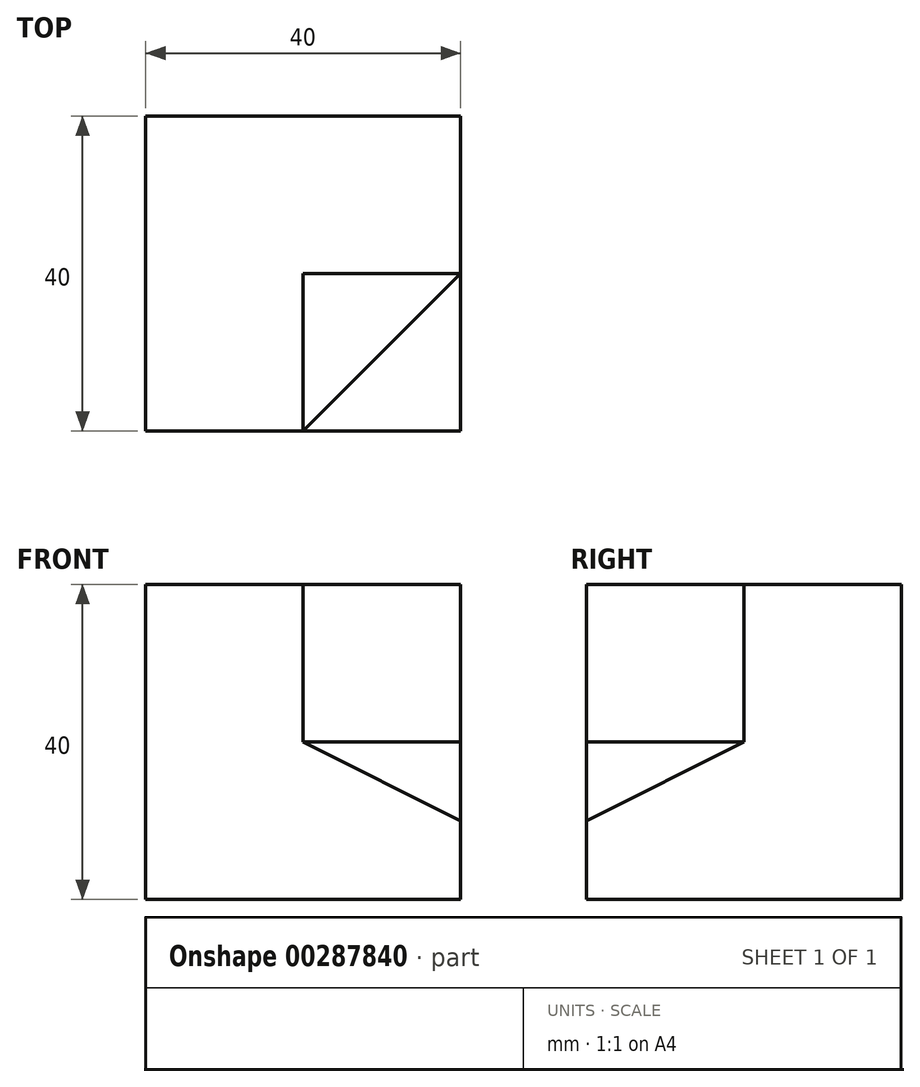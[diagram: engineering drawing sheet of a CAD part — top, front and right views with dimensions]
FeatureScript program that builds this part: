
annotation { "Feature Type Name" : "Feature", "Feature Type Description" : "" }
export const myFeature = defineFeature(function(context is Context, id is Id, definition is map)
    precondition{}
    {
        {
            var Q0;
            Q0=qCreatedBy(makeId("Front.planeOp"),FACE);
            var sketch = newSketch(context, id + "F0", { "sketchPlane" : qUnion([Q0])});
            skLineSegment(sketch, "E0.bottom", {"start": v(0, 0) * mm, "end": v(40, 0) * mm});
            skLineSegment(sketch, "E0.top", {"start": v(0, 40) * mm, "end": v(40, 40) * mm});
            skLineSegment(sketch, "E0.left", {"start": v(0, 0) * mm, "end": v(0, 40) * mm});
            skLineSegment(sketch, "E0.right", {"start": v(40, 0) * mm, "end": v(40, 40) * mm});
            skSolve(sketch);
        }
        {
            var Q0;
            Q0 = qSketchRegion(id + "F0", true);
            extrude(context, id + "F1", {"entities" : qUnion([Q0]), "depth" : 40 * mm});
        }
        {
            var Q0;
            Q0=makeQuery(id+"F1.opExtrude","CAP_FACE",FACE,{"disambiguationData":[OSD([sQuery(id+"F0.wireOp",EDGE,"E0.bottom"),sQuery(id+"F0.wireOp",EDGE,"E0.top"),sQuery(id+"F0.wireOp",EDGE,"E0.left"),sQuery(id+"F0.wireOp",EDGE,"E0.right")])],"isStart":false});
            var sketch = newSketch(context, id + "F2", { "sketchPlane" : qUnion([Q0])});
            skPoint(sketch, "E1.oppositeSnap0", {"position": v(20, 0) * mm});
            skPoint(sketch, "E1.oppositeSnap1", {"position": v(0, 20) * mm});
            skLineSegment(sketch, "E1.bottom", {"start": v(40, 40) * mm, "end": v(20, 40) * mm});
            skLineSegment(sketch, "E1.top", {"start": v(40, 20) * mm, "end": v(20, 20) * mm});
            skLineSegment(sketch, "E1.left", {"start": v(40, 40) * mm, "end": v(40, 20) * mm});
            skLineSegment(sketch, "E1.right", {"start": v(20, 40) * mm, "end": v(20, 20) * mm});
            skSolve(sketch);
        }
        {
            var Q0;
            Q0 = qSketchRegion(id + "F2", true);
            extrude(context, id + "F3", {"entities" : qUnion([Q0]), "operationType" : NewBodyOperationType.REMOVE, "oppositeDirection" : true, "depth" : 20 * mm});
        }
        {
            var Q0;
            Q0=makeQuery(id+"F1.opExtrude","CAP_EDGE",EDGE,{"disambiguationData":[OSD([sQuery(id+"F0.wireOp",EDGE,"E0.right")])],"isStart":false});
            cPoint(context, id + "F4", {"entities" : qUnion([Q0]), "parameter" : 0.5});
        }
        {
            var Q0;
            Q0=makeQuery(id+"F3.boolean.opBoolean","COPY",VERTEX,{"derivedFrom":makeQuery(id+"F3.opExtrude","CAP_VERTEX",VERTEX,{"disambiguationData":[OSD([sQuery(id+"F0.wireOp",EDGE,"E0.right"),sQuery(id+"F2.wireOp",EDGE,"E1.top"),sQuery(id+"F2.wireOp",EDGE,"E1.left")])],"isStart":false})});
            var Q1;
            Q1=makeQuery(id+"F3.boolean.opBoolean","COPY",VERTEX,{"derivedFrom":makeQuery(id+"F3.opExtrude","CAP_VERTEX",VERTEX,{"disambiguationData":[OSD([sQuery(id+"F2.wireOp",EDGE,"E1.top"),sQuery(id+"F2.wireOp",EDGE,"E1.right")])],"isStart":true})});
            var Q2;
            Q2 = qCreatedBy(id + "F4" ,VERTEX);
            cPlane(context, id + "F5", {"entities" : qUnion([Q0, Q1, Q2]), "cplaneType" : CPlaneType.THREE_POINT, "offset" : 25 * mm, "width" : 150 * mm, "height" : 150 * mm});
        }
        {
            var Q0;
            Q0=qCreatedBy(id+"F5.planeOp",FACE);
            var sketch = newSketch(context, id + "F6", { "sketchPlane" : qUnion([Q0])});
            skPoint(sketch, "E2.0", {"position": v(25.56, 8.94) * mm});
            skPoint(sketch, "E3.0", {"position": v(3.65, 26.83) * mm});
            skPoint(sketch, "E4.0", {"position": v(25.56, 31.3) * mm});
            skLineSegment(sketch, "E5", {"start": v(25.56, 8.94) * mm, "end": v(3.65, 26.83) * mm});
            skLineSegment(sketch, "E6", {"start": v(25.56, 31.3) * mm, "end": v(3.65, 26.83) * mm});
            skLineSegment(sketch, "E7", {"start": v(25.56, 8.94) * mm, "end": v(25.56, 31.3) * mm});
            skSolve(sketch);
        }
        {
            var Q0;
            Q0 = qSketchRegion(id + "F6", true);
            extrude(context, id + "F7", {"entities" : qUnion([Q0]), "operationType" : NewBodyOperationType.REMOVE, "endBound" : BoundingType.THROUGH_ALL, "oppositeDirection" : true, "depth" : 25 * mm});
        }
    });
